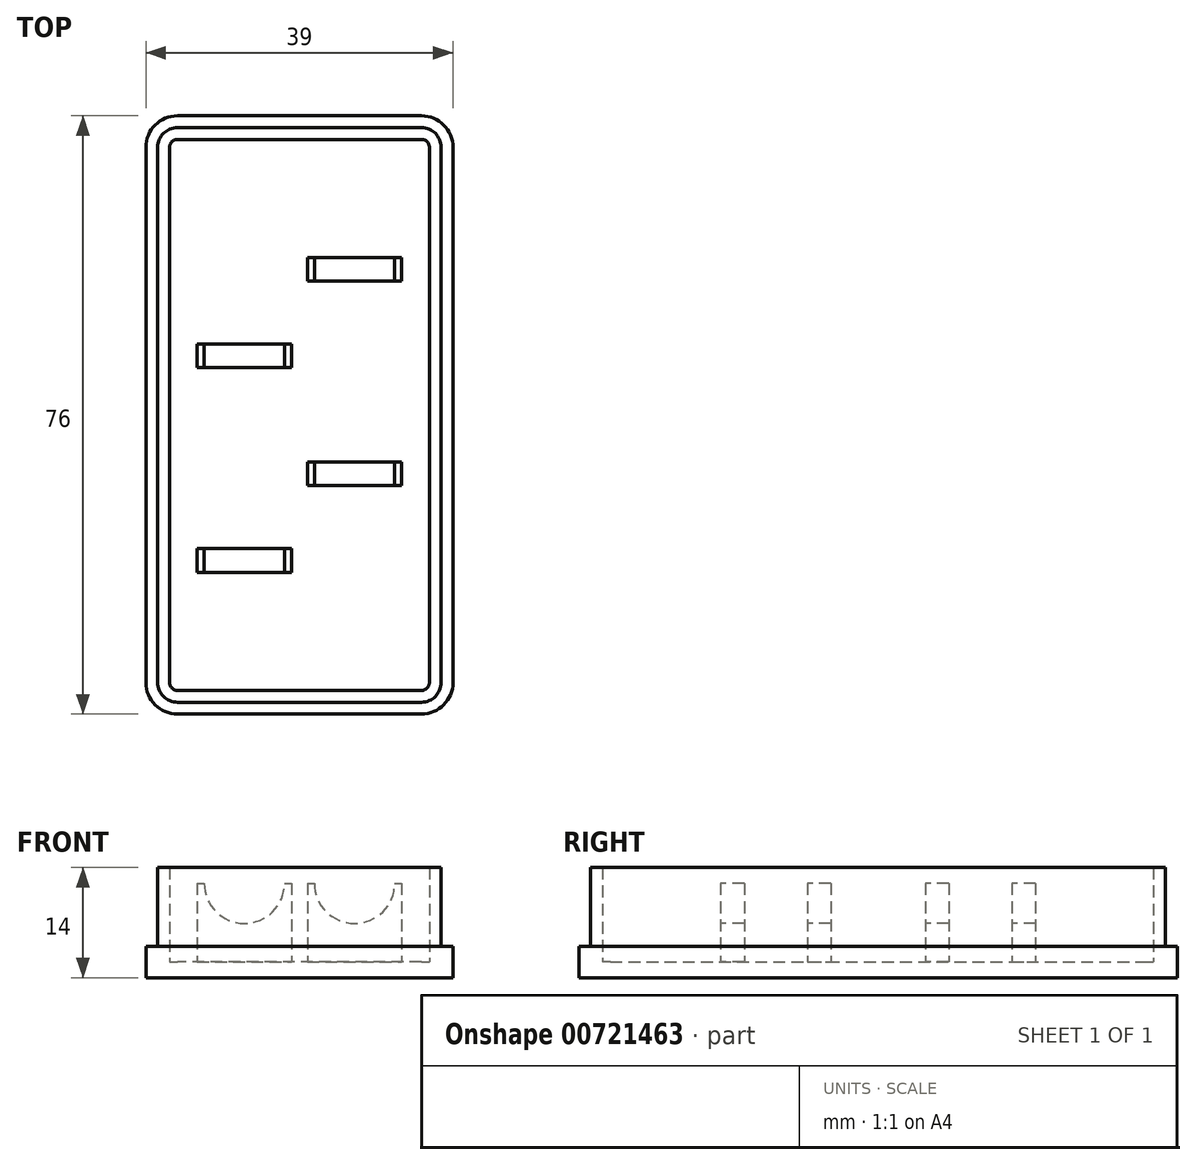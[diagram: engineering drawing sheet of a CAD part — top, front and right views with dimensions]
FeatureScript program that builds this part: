
annotation { "Feature Type Name" : "Feature", "Feature Type Description" : "" }
export const myFeature = defineFeature(function(context is Context, id is Id, definition is map)
    precondition{}
    {
        {
            var Q0;
            Q0=qCreatedBy(makeId("Top.planeOp"),FACE);
            var sketch = newSketch(context, id + "F0", { "sketchPlane" : qUnion([Q0])});
            skLineSegment(sketch, "E0.bottom", {"start": v(15.5, -38) * mm, "end": v(-15.5, -38) * mm});
            skLineSegment(sketch, "E0.top", {"start": v(15.5, 38) * mm, "end": v(-15.5, 38) * mm});
            skLineSegment(sketch, "E0.left", {"start": v(19.5, -34) * mm, "end": v(19.5, 34) * mm});
            skLineSegment(sketch, "E0.right", {"start": v(-19.5, -34) * mm, "end": v(-19.5, 34) * mm});
            skPoint(sketch, "E0.middle", {"position": v(0, 0) * mm});
            skPoint(sketch, "E1.visualSharp", {"position": v(-19.5, 38) * mm});
            skArc(sketch, "E1.filletArc", {"start": v(-15.5, 38) * mm, "mid": v(-18.33, 36.83) * mm, "end": v(-19.5, 34) * mm});
            skPoint(sketch, "E2.visualSharp", {"position": v(19.5, 38) * mm});
            skArc(sketch, "E2.filletArc", {"start": v(19.5, 34) * mm, "mid": v(18.33, 36.83) * mm, "end": v(15.5, 38) * mm});
            skPoint(sketch, "E3.visualSharp", {"position": v(-19.5, -38) * mm});
            skArc(sketch, "E3.filletArc", {"start": v(-19.5, -34) * mm, "mid": v(-18.33, -36.83) * mm, "end": v(-15.5, -38) * mm});
            skPoint(sketch, "E4.visualSharp", {"position": v(19.5, -38) * mm});
            skArc(sketch, "E4.filletArc", {"start": v(15.5, -38) * mm, "mid": v(18.33, -36.83) * mm, "end": v(19.5, -34) * mm});
            skSolve(sketch);
        }
        {
            var Q0;
            Q0 = qSketchRegion(id + "F0", true);
            extrude(context, id + "F1", {"entities" : qUnion([Q0]), "depth" : 2 * mm, "offsetDistance" : 25 * mm});
        }
        {
            var Q0;
            Q0=makeQuery(id+"F1.opExtrude","CAP_FACE",FACE,{"disambiguationData":[OSD([sQuery(id+"F0.wireOp",EDGE,"E0.bottom"),sQuery(id+"F0.wireOp",EDGE,"E0.top"),sQuery(id+"F0.wireOp",EDGE,"E0.left"),sQuery(id+"F0.wireOp",EDGE,"E0.right"),sQuery(id+"F0.wireOp",EDGE,"E1.filletArc"),sQuery(id+"F0.wireOp",EDGE,"E2.filletArc"),sQuery(id+"F0.wireOp",EDGE,"E3.filletArc"),sQuery(id+"F0.wireOp",EDGE,"E4.filletArc")])],"isStart":false});
            var sketch = newSketch(context, id + "F2", { "sketchPlane" : qUnion([Q0])});
            skLineSegment(sketch, "E5.0", {"start": v(-19.5, -34) * mm, "end": v(-19.5, 34) * mm});
            skLineSegment(sketch, "E6.0", {"start": v(19.5, -34) * mm, "end": v(19.5, 34) * mm});
            skArc(sketch, "E7.0", {"start": v(19.5, 34) * mm, "mid": v(18.33, 36.83) * mm, "end": v(15.5, 38) * mm});
            skLineSegment(sketch, "E8.0", {"start": v(15.5, 38) * mm, "end": v(-15.5, 38) * mm});
            skArc(sketch, "E9.0", {"start": v(-15.5, 38) * mm, "mid": v(-18.33, 36.83) * mm, "end": v(-19.5, 34) * mm});
            skLineSegment(sketch, "E10.0", {"start": v(15.5, -38) * mm, "end": v(-15.5, -38) * mm});
            skArc(sketch, "E11.0", {"start": v(15.5, -38) * mm, "mid": v(18.33, -36.83) * mm, "end": v(19.5, -34) * mm});
            skArc(sketch, "E12.0", {"start": v(-19.5, -34) * mm, "mid": v(-18.33, -36.83) * mm, "end": v(-15.5, -38) * mm});
            skArc(sketch, "E13.0", {"start": v(-16.5, -34) * mm, "mid": v(-16.2, -34.7) * mm, "end": v(-15.5, -35) * mm});
            skLineSegment(sketch, "E13.1", {"start": v(15.5, -35) * mm, "end": v(-15.5, -35) * mm});
            skLineSegment(sketch, "E13.2", {"start": v(-16.5, -34) * mm, "end": v(-16.5, 34) * mm});
            skArc(sketch, "E13.3", {"start": v(15.5, -35) * mm, "mid": v(16.2, -34.7) * mm, "end": v(16.5, -34) * mm});
            skArc(sketch, "E13.4", {"start": v(-15.5, 35) * mm, "mid": v(-16.2, 34.7) * mm, "end": v(-16.5, 34) * mm});
            skLineSegment(sketch, "E13.5", {"start": v(15.5, 35) * mm, "end": v(-15.5, 35) * mm});
            skArc(sketch, "E13.6", {"start": v(16.5, 34) * mm, "mid": v(16.2, 34.7) * mm, "end": v(15.5, 35) * mm});
            skLineSegment(sketch, "E13.7", {"start": v(16.5, -34) * mm, "end": v(16.5, 34) * mm});
            skSolve(sketch);
        }
        {
            var Q0;
            Q0 = qSketchRegion(id + "F2", true);
            extrude(context, id + "F3", {"entities" : qUnion([Q0]), "operationType" : NewBodyOperationType.ADD, "depth" : 2 * mm, "offsetDistance" : 25 * mm});
        }
        {
            var Q0;
            Q0=makeQuery(id+"F3.opExtrude","CAP_FACE",FACE,{"disambiguationData":[OSD([sQuery(id+"F2.wireOp",EDGE,"E5.0"),sQuery(id+"F2.wireOp",EDGE,"E6.0"),sQuery(id+"F2.wireOp",EDGE,"E7.0"),sQuery(id+"F2.wireOp",EDGE,"E8.0"),sQuery(id+"F2.wireOp",EDGE,"E9.0"),sQuery(id+"F2.wireOp",EDGE,"E10.0"),sQuery(id+"F2.wireOp",EDGE,"E11.0"),sQuery(id+"F2.wireOp",EDGE,"E12.0"),sQuery(id+"F2.wireOp",EDGE,"E13.0"),sQuery(id+"F2.wireOp",EDGE,"E13.1"),sQuery(id+"F2.wireOp",EDGE,"E13.2"),sQuery(id+"F2.wireOp",EDGE,"E13.3"),sQuery(id+"F2.wireOp",EDGE,"E13.4"),sQuery(id+"F2.wireOp",EDGE,"E13.5"),sQuery(id+"F2.wireOp",EDGE,"E13.6"),sQuery(id+"F2.wireOp",EDGE,"E13.7")])],"isStart":false});
            var sketch = newSketch(context, id + "F4", { "sketchPlane" : qUnion([Q0])});
            skArc(sketch, "E14.0", {"start": v(-16.5, -34) * mm, "mid": v(-16.2, -34.7) * mm, "end": v(-15.5, -35) * mm});
            skLineSegment(sketch, "E14.1", {"start": v(15.5, -35) * mm, "end": v(-15.5, -35) * mm});
            skLineSegment(sketch, "E14.2", {"start": v(-16.5, -34) * mm, "end": v(-16.5, 34) * mm});
            skArc(sketch, "E14.3", {"start": v(15.5, -35) * mm, "mid": v(16.2, -34.7) * mm, "end": v(16.5, -34) * mm});
            skArc(sketch, "E14.4", {"start": v(-15.5, 35) * mm, "mid": v(-16.2, 34.7) * mm, "end": v(-16.5, 34) * mm});
            skLineSegment(sketch, "E14.5", {"start": v(15.5, 35) * mm, "end": v(-15.5, 35) * mm});
            skArc(sketch, "E14.6", {"start": v(16.5, 34) * mm, "mid": v(16.2, 34.7) * mm, "end": v(15.5, 35) * mm});
            skLineSegment(sketch, "E14.7", {"start": v(16.5, -34) * mm, "end": v(16.5, 34) * mm});
            skArc(sketch, "E15.0", {"start": v(-18, -34) * mm, "mid": v(-17.27, -35.77) * mm, "end": v(-15.5, -36.5) * mm});
            skLineSegment(sketch, "E15.1", {"start": v(15.5, -36.5) * mm, "end": v(-15.5, -36.5) * mm});
            skLineSegment(sketch, "E15.2", {"start": v(-18, -34) * mm, "end": v(-18, 34) * mm});
            skArc(sketch, "E15.3", {"start": v(15.5, -36.5) * mm, "mid": v(17.27, -35.77) * mm, "end": v(18, -34) * mm});
            skArc(sketch, "E15.4", {"start": v(-15.5, 36.5) * mm, "mid": v(-17.27, 35.77) * mm, "end": v(-18, 34) * mm});
            skLineSegment(sketch, "E15.5", {"start": v(15.5, 36.5) * mm, "end": v(-15.5, 36.5) * mm});
            skArc(sketch, "E15.6", {"start": v(18, 34) * mm, "mid": v(17.27, 35.77) * mm, "end": v(15.5, 36.5) * mm});
            skLineSegment(sketch, "E15.7", {"start": v(18, -34) * mm, "end": v(18, 34) * mm});
            skSolve(sketch);
        }
        {
            var Q0;
            Q0=makeQuery(id+"F4.imprint","IMPRINT",FACE,{"disambiguationData":[TD([[makeQuery(id+"F4.imprint","IMPRINT",EDGE,{"derivedFrom":sQuery(id+"F4.wireOp",EDGE,"E14.0")}),1.0]])]});
            var sketch = newSketch(context, id + "F5", { "sketchPlane" : qUnion([Q0])});
            skLineSegment(sketch, "E16", {"start": v(-7, 48.7) * mm, "end": v(-7, -33.46) * mm, "construction": true});
            skLineSegment(sketch, "E17.bottom", {"start": v(-1, -17) * mm, "end": v(-13, -17) * mm});
            skLineSegment(sketch, "E17.top", {"start": v(-1, -20) * mm, "end": v(-13, -20) * mm});
            skLineSegment(sketch, "E17.left", {"start": v(-1, -17) * mm, "end": v(-1, -20) * mm});
            skLineSegment(sketch, "E17.right", {"start": v(-13, -17) * mm, "end": v(-13, -20) * mm});
            skPoint(sketch, "E17.middle", {"position": v(-7, -18.5) * mm});
            skLineSegment(sketch, "E18.bottom", {"start": v(-13, 9) * mm, "end": v(-1, 9) * mm});
            skLineSegment(sketch, "E18.top", {"start": v(-13, 6) * mm, "end": v(-1, 6) * mm});
            skLineSegment(sketch, "E18.left", {"start": v(-13, 9) * mm, "end": v(-13, 6) * mm});
            skLineSegment(sketch, "E18.right", {"start": v(-1, 9) * mm, "end": v(-1, 6) * mm});
            skPoint(sketch, "E18.middle", {"position": v(-7, 7.5) * mm});
            skLineSegment(sketch, "E19", {"start": v(0, 46.25) * mm, "end": v(0, -45.18) * mm, "construction": true});
            skLineSegment(sketch, "E20.MirrorCS", {"start": v(7, 48.7) * mm, "end": v(7, -33.46) * mm, "construction": true});
            skLineSegment(sketch, "E21.bottom", {"start": v(1, 17) * mm, "end": v(13, 17) * mm});
            skLineSegment(sketch, "E21.top", {"start": v(1, 20) * mm, "end": v(13, 20) * mm});
            skLineSegment(sketch, "E21.left", {"start": v(1, 17) * mm, "end": v(1, 20) * mm});
            skLineSegment(sketch, "E21.right", {"start": v(13, 17) * mm, "end": v(13, 20) * mm});
            skPoint(sketch, "E21.middle", {"position": v(7, 18.5) * mm});
            skLineSegment(sketch, "E22.bottom", {"start": v(1, -9) * mm, "end": v(13, -9) * mm});
            skLineSegment(sketch, "E22.top", {"start": v(1, -6) * mm, "end": v(13, -6) * mm});
            skLineSegment(sketch, "E22.left", {"start": v(1, -9) * mm, "end": v(1, -6) * mm});
            skLineSegment(sketch, "E22.right", {"start": v(13, -9) * mm, "end": v(13, -6) * mm});
            skPoint(sketch, "E22.middle", {"position": v(7, -7.5) * mm});
            skSolve(sketch);
        }
        {
            var Q0;
            Q0 = qSketchRegion(id + "F5", true);
            extrude(context, id + "F6", {"entities" : qUnion([Q0]), "depth" : 8 * mm, "offsetDistance" : 25 * mm, "hasSecondDirection" : true, "secondDirectionOppositeDirection" : true, "secondDirectionDepth" : 2 * mm});
        }
        {
            var Q0;
            Q0=makeQuery(id+"F6.opExtrude","SWEPT_FACE",FACE,{"disambiguationData":[OSD([sQuery(id+"F5.wireOp",EDGE,"E17.top")])]});
            var sketch = newSketch(context, id + "F7", { "sketchPlane" : qUnion([Q0])});
            skArc(sketch, "E23", {"start": v(-12.1, 12) * mm, "mid": v(-7, 6.9) * mm, "end": v(-1.9, 12) * mm});
            skLineSegment(sketch, "E24", {"start": v(-12.1, 12) * mm, "end": v(-1.9, 12) * mm});
            skSolve(sketch);
        }
        {
            var Q0;
            Q0 = qSketchRegion(id + "F7", true);
            extrude(context, id + "F8", {"entities" : qUnion([Q0]), "operationType" : NewBodyOperationType.REMOVE, "oppositeDirection" : true, "depth" : 50 * mm, "offsetDistance" : 25 * mm});
        }
        {
            var Q0;
            Q0=makeQuery(id+"F6.opExtrude","SWEPT_FACE",FACE,{"disambiguationData":[OSD([sQuery(id+"F5.wireOp",EDGE,"E22.bottom")])]});
            var sketch = newSketch(context, id + "F9", { "sketchPlane" : qUnion([Q0])});
            skArc(sketch, "E25", {"start": v(1.9, 12) * mm, "mid": v(7, 6.9) * mm, "end": v(12.1, 12) * mm});
            skLineSegment(sketch, "E26", {"start": v(1.9, 12) * mm, "end": v(12.1, 12) * mm});
            skSolve(sketch);
        }
        {
            var Q0;
            Q0 = qSketchRegion(id + "F9", true);
            extrude(context, id + "F10", {"entities" : qUnion([Q0]), "operationType" : NewBodyOperationType.REMOVE, "oppositeDirection" : true, "depth" : 50 * mm, "offsetDistance" : 25 * mm});
        }
        {
            var Q0;
            Q0 = qSketchRegion(id + "F4", true);
            extrude(context, id + "F11", {"entities" : qUnion([Q0]), "operationType" : NewBodyOperationType.ADD, "depth" : 10 * mm, "offsetDistance" : 25 * mm});
        }
    });
